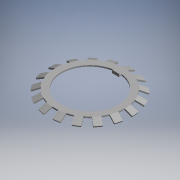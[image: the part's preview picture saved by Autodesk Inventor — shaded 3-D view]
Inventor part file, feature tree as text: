
AUTODESK INVENTOR PART (.ipt)
format: ipt  version: 2017.3 (Build 213256000, 256)  size: 276,992 bytes
history: native  units: mm (DEFAULTED — no unit token found)
features: other x7, sketch x3, extrude x2, revolve x1
ambient origin geometry x8: Origin, YZ Plane, XZ Plane, XY Plane, X Axis, Y Axis, Z Axis, Center Point
bodies: Solid1 (feature_tree)
feature tree (13):
  revolve  "Revolution1"  [1 undecoded]
  extrude  "Extrusion1"  TaperAngle=0.0deg  [1 undecoded]
  extrude  "Extrusion2"  [1 undecoded]
  other  "washer_XY"
  other  "washer_YZ"
  other  "washer_ZX"
  other  "washer_X"
  other  "washer_Y"
  other  "washer_Z"
  other  "washer_Center"
  sketch  "Sketch_1"  dims[d0=360.0deg d1=6.0mm d2=0.0mm]
  sketch  "Sketch_2"  dims[d3=20.0mm d4=0.0mm d5=0.0mm]
  sketch  "Sketch_3"
note: 3 required parameter values undecoded (feature->parameter linkage not recoverable at this tier; creation-order binding heuristic only, values carry confidence <= 0.55)